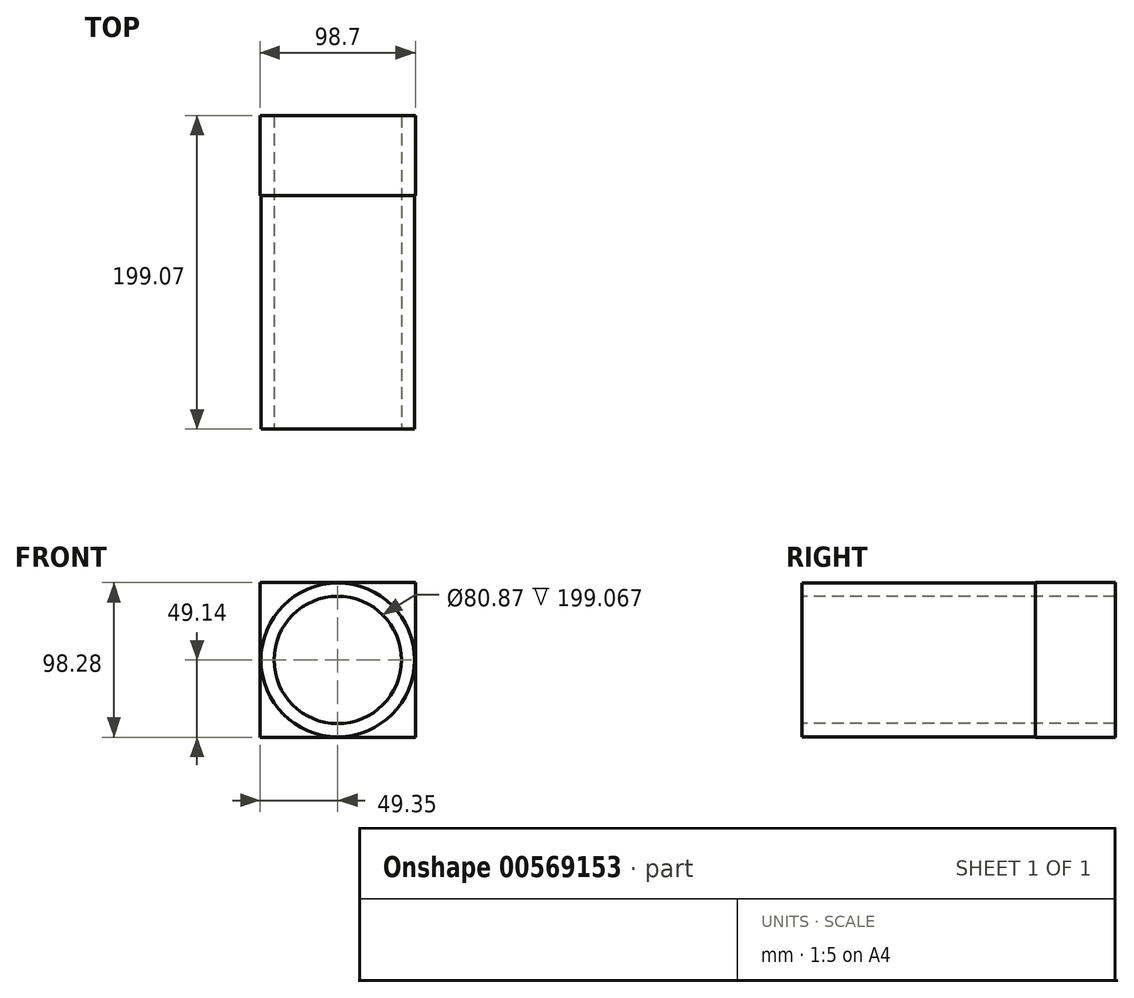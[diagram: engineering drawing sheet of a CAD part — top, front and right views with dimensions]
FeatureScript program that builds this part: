
annotation { "Feature Type Name" : "Feature", "Feature Type Description" : "" }
export const myFeature = defineFeature(function(context is Context, id is Id, definition is map)
    precondition{}
    {
        {
            var Q0;
            Q0=qCreatedBy(makeId("Front.planeOp"),FACE);
            var sketch = newSketch(context, id + "F0", { "sketchPlane" : qUnion([Q0])});
            skLineSegment(sketch, "E0.bottom", {"start": v(49.35, 49.14) * mm, "end": v(-49.35, 49.14) * mm});
            skLineSegment(sketch, "E0.top", {"start": v(49.35, -49.14) * mm, "end": v(-49.35, -49.14) * mm});
            skLineSegment(sketch, "E0.left", {"start": v(49.35, 49.14) * mm, "end": v(49.35, -49.14) * mm});
            skLineSegment(sketch, "E0.right", {"start": v(-49.35, 49.14) * mm, "end": v(-49.35, -49.14) * mm});
            skPoint(sketch, "E0.middle", {"position": v(0, 0) * mm});
            skCircle(sketch, "E1", {"center": v(0, 0) * mm, "radius": 40.43 * mm});
            skSolve(sketch);
        }
        {
            var Q0;
            Q0 = qSketchRegion(id + "F0", true);
            extrude(context, id + "F1", {"entities" : qUnion([Q0]), "oppositeDirection" : true, "depth" : 50.8 * mm, "offsetDistance" : 25.4 * mm});
        }
        {
            var Q0;
            Q0=makeQuery(id+"F1.opExtrude","CAP_FACE",FACE,{"disambiguationData":[OSD([sQuery(id+"F0.wireOp",EDGE,"E0.bottom"),sQuery(id+"F0.wireOp",EDGE,"E0.top"),sQuery(id+"F0.wireOp",EDGE,"E0.left"),sQuery(id+"F0.wireOp",EDGE,"E0.right"),sQuery(id+"F0.wireOp",EDGE,"E1")])],"isStart":true});
            var sketch = newSketch(context, id + "F2", { "sketchPlane" : qUnion([Q0])});
            skCircle(sketch, "E2.0", {"center": v(0, 0) * mm, "radius": 40.43 * mm});
            skCircle(sketch, "E3.0", {"center": v(0, 0) * mm, "radius": 48.82 * mm});
            skSolve(sketch);
        }
        {
            var Q0;
            Q0 = qSketchRegion(id + "F2", true);
            extrude(context, id + "F3", {"entities" : qUnion([Q0]), "operationType" : NewBodyOperationType.ADD, "endBound" : BoundingType.THROUGH_ALL, "depth" : 50.8 * mm, "offsetDistance" : 25.4 * mm});
        }
    });
